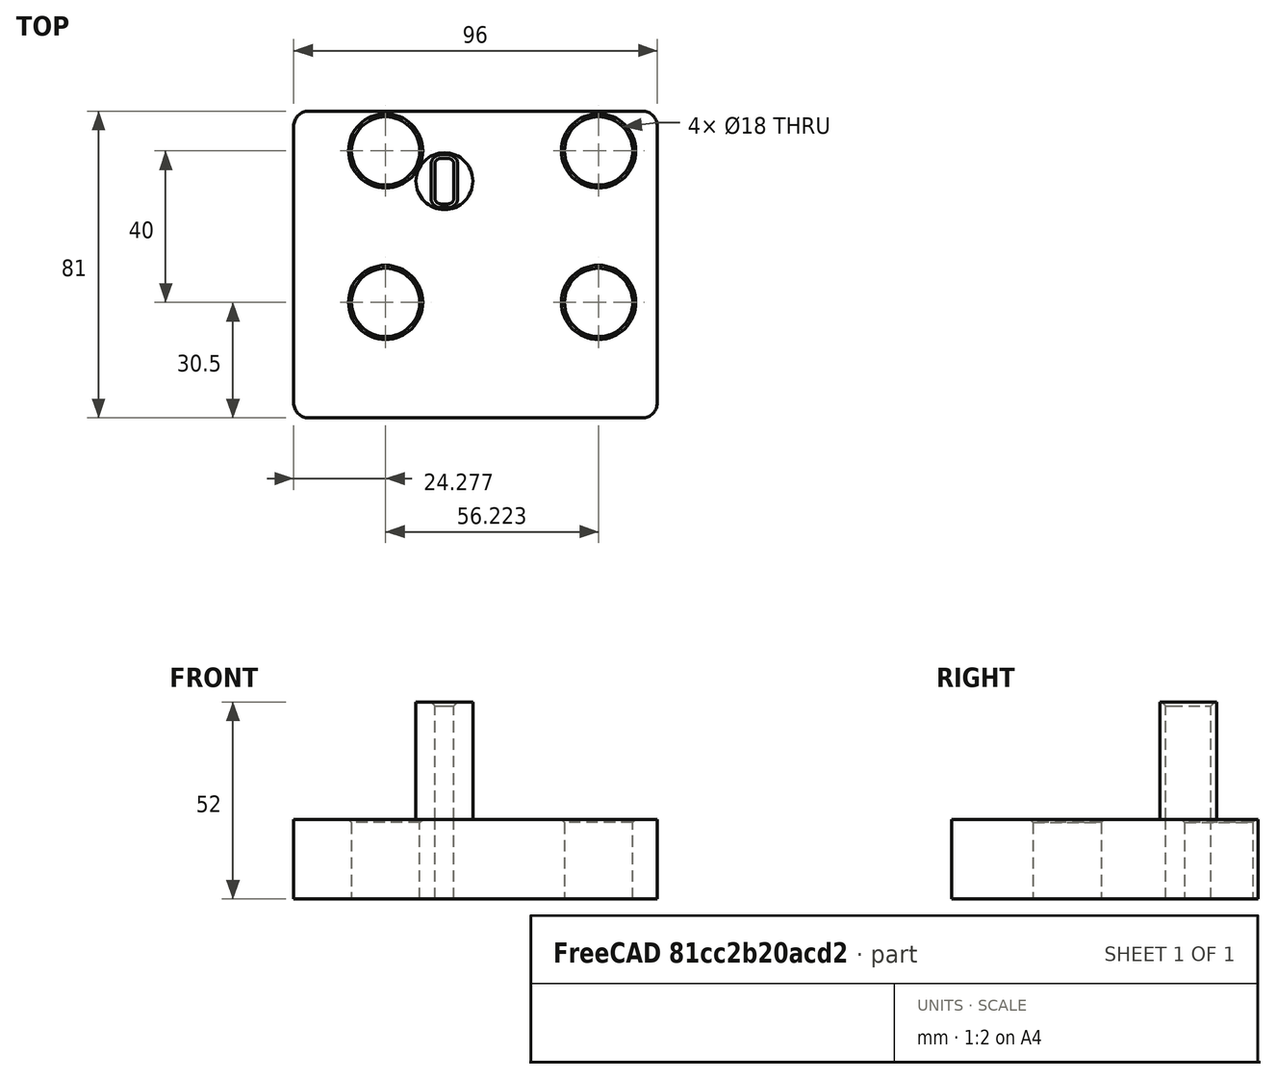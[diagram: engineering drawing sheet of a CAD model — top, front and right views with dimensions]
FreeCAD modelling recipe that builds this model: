
FCSTD DOCUMENT  (FreeCAD 0.21R33694 (Git))
Label: mercedes_lock_yobana_rot
License: All rights reserved
LicenseURL: http://en.wikipedia.org/wiki/All_rights_reserved
objects: Sketcher::SketchObject×3, PartDesign::Pad×2, PartDesign::Fillet×2, PartDesign::Chamfer×2, PartDesign::Pocket×1, PartDesign::Body×1, Mesh::Feature×1
note: 18 computed .brp shape members not serialized (recipe doc carries the construction recipe); baked Part::Feature solids carry a one-line shape summary decoded from their .brp

FEATURE [Sketcher::SketchObject] Sketch
  FullyConstrained = true
  MapMode = 5
  Support = -> [XY_Plane]
  expr: Constraints[14] = 80 - 11
  expr: Constraints[15] = 80 - 11
  expr: Constraints[16] = 10 + 11 / 2
  expr: Constraints[17] = 10 + 11 / 2
  expr: Constraints[20] = 5 + 11 / 2
  expr: Constraints[21] = 5 + 11 / 2
  sketch-geometry (8):
    g0: LineSegment StartX=-48 StartY=40.5 StartZ=0 EndX=48 EndY=40.5 EndZ=0
    g1: LineSegment StartX=48 StartY=40.5 StartZ=0 EndX=48 EndY=-40.5 EndZ=0
    g2: LineSegment StartX=-48 StartY=-40.5 StartZ=0 EndX=48 EndY=-40.5 EndZ=0
    g3: LineSegment StartX=-48 StartY=40.5 StartZ=0 EndX=-48 EndY=-40.5 EndZ=0
    g4: Circle CenterX=-23.7228 CenterY=30 CenterZ=0 NormalX=0 NormalY=0 NormalZ=1 AngleXU=0 Radius=9
    g5: Circle CenterX=32.5 CenterY=30 CenterZ=0 NormalX=0 NormalY=0 NormalZ=1 AngleXU=0 Radius=9
    g6: Circle CenterX=-23.7228 CenterY=-10 CenterZ=0 NormalX=0 NormalY=0 NormalZ=1 AngleXU=0 Radius=9
    g7: Circle CenterX=32.5 CenterY=-10 CenterZ=0 NormalX=0 NormalY=0 NormalZ=1 AngleXU=0 Radius=9
  constraints (22):
    c: Coincident(g3,g0)
    c: Coincident(g3,g2)
    c: Coincident(g2,g1)
    c: Coincident(g0,g1)
    c: Equal(g5,g7)
    c: Equal(g7,g6)
    c: Equal(g6,g4)
    c: Equal(g1,g3)
    c: Equal(g0,g2)
    c: Distance(g1) = 81
    c: Distance(g0) = 96
    c: Symmetric(g0,g2,g-1)
    c: Symmetric(g0,g2,g-1)
    c: Diameter(g5) = 18
    c: Distance(g7,g4) = 69
    c: Distance(g6,g5) = 69
    c: Distance(g5,g1) = 15.5
    c: Distance(g7,g1) = 15.5
    c: Distance(g5,g7) = 40
    c: Distance(g4,g6) = 40
    c: Distance(g5,g0) = 10.5
    c: Distance(g4,g0) = 10.5
FEATURE [PartDesign::Pad] Pad
  Direction = (0,0,1)
  Length = 21
  Length2 = 10
  Profile = -> Sketch
  ReferenceAxis = -> Sketch [N_Axis]
  Type = 0
FEATURE [Sketcher::SketchObject] Sketch001
  ExternalGeometry = -> [Pad]
  FullyConstrained = true
  MapMode = 5
  Placement = pos=(0,0,21) rot=(0,0,1;0rad)
  Support = -> [Pad]
  expr: Constraints[16] = 54 + 2.2
  expr: Constraints[17] = 12 + 13 / 2
  sketch-geometry (7):
    g0: LineSegment StartX=-10.7 StartY=28 StartZ=0 EndX=-10.7 EndY=16 EndZ=0
    g1: LineSegment StartX=-10.7 StartY=16 StartZ=0 EndX=-5.7 EndY=16 EndZ=0
    g2: LineSegment StartX=-5.7 StartY=16 StartZ=0 EndX=-5.7 EndY=28 EndZ=0
    g3: LineSegment StartX=-10.7 StartY=28 StartZ=0 EndX=-5.7 EndY=28 EndZ=0
    g4: LineSegment StartX=-5.7 StartY=28 StartZ=0 EndX=-10.7 EndY=16 EndZ=0
    g5: LineSegment StartX=-10.7 StartY=28 StartZ=0 EndX=-5.7 EndY=16 EndZ=0
    g6: GeomPoint X=-8.2 Y=22 Z=0
  constraints (18):
    c: Coincident(g2,g3)
    c: Coincident(g0,g3)
    c: Coincident(g0,g1)
    c: Coincident(g1,g2)
    c: Parallel(g0,g2)
    c: Parallel(g2,g-2)
    c: Parallel(g3,g1)
    c: Parallel(g1,g-1)
    c: DistanceX(g0,g1) = 5
    c: Distance(g2,g1) = 12
    c: Coincident(g4,g2)
    c: Coincident(g4,g0)
    c: Coincident(g5,g0)
    c: Coincident(g5,g1)
    c: PointOnObject(g6,g4)
    c: PointOnObject(g6,g5)
    c: Distance(g6,g-4) = 56.2
    c: Distance(g6,g-3) = 18.5
FEATURE [PartDesign::Pocket] Pocket
  BaseFeature = -> Pad
  Direction = (0,0,-1)
  Length = 5
  Length2 = 5
  Profile = -> Sketch001
  ReferenceAxis = -> Sketch001 [N_Axis]
  Type = 1
FEATURE [Sketcher::SketchObject] Sketch002
  ExternalGeometry = -> [Pocket]
  FullyConstrained = true
  MapMode = 5
  Placement = pos=(0,0,21) rot=(0,0,1;0rad)
  Support = -> [Pocket]
  sketch-geometry (8):
    g0: LineSegment StartX=-5.7 StartY=28 StartZ=0 EndX=-10.7 EndY=16 EndZ=0
    g1: LineSegment StartX=-10.7 StartY=28 StartZ=0 EndX=-5.7 EndY=16 EndZ=0
    g2: GeomPoint X=-8.2 Y=22 Z=0
    g3: Circle CenterX=-8.2 CenterY=22 CenterZ=0 NormalX=0 NormalY=0 NormalZ=1 AngleXU=0 Radius=7.5
    g4: LineSegment StartX=-10.7 StartY=28 StartZ=0 EndX=-5.7 EndY=28 EndZ=0
    g5: LineSegment StartX=-5.7 StartY=28 StartZ=0 EndX=-5.7 EndY=16 EndZ=0
    g6: LineSegment StartX=-10.7 StartY=16 StartZ=0 EndX=-5.7 EndY=16 EndZ=0
    g7: LineSegment StartX=-10.7 StartY=16 StartZ=0 EndX=-10.7 EndY=28 EndZ=0
  constraints (16):
    c: Coincident(g0,g-4)
    c: Coincident(g0,g-5)
    c: Coincident(g1,g-5)
    c: Coincident(g1,g-4)
    c: PointOnObject(g2,g0)
    c: PointOnObject(g2,g1)
    c: Coincident(g3,g2)
    c: Diameter(g3) = 15  '14.5'
    c: Coincident(g7,g4)
    c: Coincident(g4,g5)
    c: Coincident(g6,g5)
    c: Coincident(g6,g7)
    c: Coincident(g4,g1)
    c: Coincident(g4,g0)
    c: Coincident(g5,g1)
    c: Coincident(g6,g0)
FEATURE [PartDesign::Pad] Pad001
  BaseFeature = -> Pocket
  Direction = (0,0,1)
  Length = 31
  Length2 = 10
  Profile = -> Sketch002
  ReferenceAxis = -> Sketch002 [N_Axis]
  Type = 0
FEATURE [PartDesign::Fillet] Fillet
  Base = -> Pad001 [Edge1,Edge5,Edge8,Edge2]
  BaseFeature = -> Pad001
  Radius = 4
  SupportTransform = false
  UseAllEdges = false
FEATURE [PartDesign::Fillet] Fillet001
  Base = -> Fillet [Edge52,Edge55,Edge53,Edge57]
  BaseFeature = -> Fillet
  Radius = 1.5
  SupportTransform = false
  UseAllEdges = false
FEATURE [PartDesign::Chamfer] Chamfer
  Angle = 45
  Base = -> Fillet001 [Edge76]
  BaseFeature = -> Fillet001
  ChamferType = 0
  FlipDirection = false
  Size = 1
  Size2 = 1
  SupportTransform = false
  UseAllEdges = false
FEATURE [PartDesign::Chamfer] Chamfer001
  Angle = 45
  Base = -> Chamfer [Edge92,Edge94,Edge90,Edge88]
  BaseFeature = -> Chamfer
  ChamferType = 0
  FlipDirection = false
  Size = 0.8
  Size2 = 1
  SupportTransform = false
  UseAllEdges = false
FEATURE [PartDesign::Body] Body
  Group = -> [Sketch,Pad,Sketch001,Pocket,Sketch002,Pad001,Fillet,Fillet001,Chamfer,Chamfer001]
  Origin = -> Origin
  Tip = -> Chamfer001
FEATURE [Mesh::Feature] Mesh  label="Mercedes_lock_bone"
